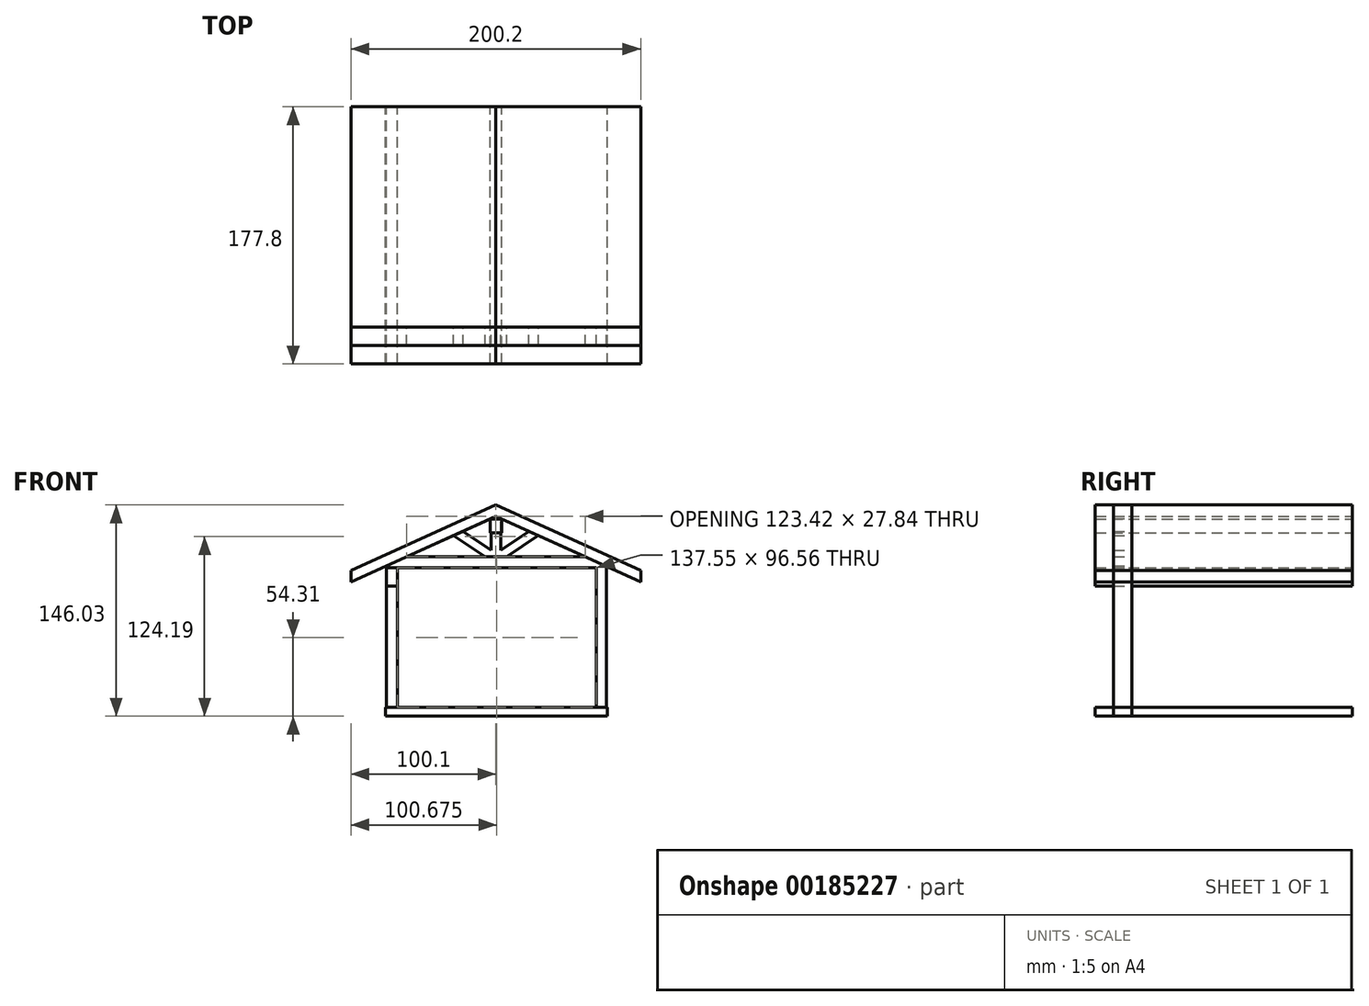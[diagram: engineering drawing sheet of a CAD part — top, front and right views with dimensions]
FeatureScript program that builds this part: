
annotation { "Feature Type Name" : "Feature", "Feature Type Description" : "" }
export const myFeature = defineFeature(function(context is Context, id is Id, definition is map)
    precondition{}
    {
        {
            var Q0;
            Q0=qCreatedBy(makeId("Front.planeOp"),FACE);
            var sketch = newSketch(context, id + "F0", { "sketchPlane" : qUnion([Q0])});
            skLineSegment(sketch, "E0.bottom", {"start": v(-76.23, -56.3) * mm, "end": v(77.09, -56.3) * mm});
            skLineSegment(sketch, "E0.top", {"start": v(-76.23, -62.33) * mm, "end": v(77.09, -62.33) * mm});
            skLineSegment(sketch, "E0.left", {"start": v(-76.23, -56.3) * mm, "end": v(-76.23, -62.33) * mm});
            skLineSegment(sketch, "E0.right", {"start": v(77.09, -56.3) * mm, "end": v(77.09, -62.33) * mm});
            skLineSegment(sketch, "E1.bottom", {"start": v(-75.65, 27.65) * mm, "end": v(-68.2, 27.65) * mm});
            skLineSegment(sketch, "E1.top", {"start": v(-75.65, -56.3) * mm, "end": v(-68.2, -56.3) * mm});
            skLineSegment(sketch, "E1.left", {"start": v(-75.65, 27.65) * mm, "end": v(-75.65, -56.3) * mm});
            skLineSegment(sketch, "E1.right", {"start": v(-68.2, 27.65) * mm, "end": v(-68.2, -56.3) * mm});
            skLineSegment(sketch, "E2.bottom", {"start": v(76.51, 25.93) * mm, "end": v(69.35, 25.93) * mm});
            skLineSegment(sketch, "E2.top", {"start": v(76.51, -56.3) * mm, "end": v(69.35, -56.3) * mm});
            skLineSegment(sketch, "E2.left", {"start": v(76.51, 25.93) * mm, "end": v(76.51, -56.3) * mm});
            skLineSegment(sketch, "E2.right", {"start": v(69.35, 25.93) * mm, "end": v(69.35, -56.3) * mm});
            skLineSegment(sketch, "E3.bottom", {"start": v(-75.65, 27.65) * mm, "end": v(-75.65, 27.65) * mm});
            skLineSegment(sketch, "E3.top", {"start": v(-75.65, 40.26) * mm, "end": v(-75.65, 40.26) * mm});
            skLineSegment(sketch, "E3.left", {"start": v(-75.65, 27.65) * mm, "end": v(-75.65, 40.26) * mm});
            skLineSegment(sketch, "E3.right", {"start": v(-75.65, 27.65) * mm, "end": v(-75.65, 40.26) * mm});
            skLineSegment(sketch, "E4.bottom", {"start": v(69.35, 40.26) * mm, "end": v(76.51, 40.26) * mm});
            skLineSegment(sketch, "E4.top", {"start": v(69.35, 25.93) * mm, "end": v(76.51, 25.93) * mm});
            skLineSegment(sketch, "E4.left", {"start": v(69.35, 40.26) * mm, "end": v(69.35, 25.93) * mm});
            skLineSegment(sketch, "E4.right", {"start": v(76.51, 40.26) * mm, "end": v(76.51, 25.93) * mm});
            skLineSegment(sketch, "E5.bottom", {"start": v(-75.65, 40.26) * mm, "end": v(76.51, 40.26) * mm});
            skLineSegment(sketch, "E5.top", {"start": v(-75.65, 47.94) * mm, "end": v(76.51, 47.94) * mm});
            skLineSegment(sketch, "E5.left", {"start": v(-75.65, 40.26) * mm, "end": v(-75.65, 47.94) * mm});
            skLineSegment(sketch, "E5.right", {"start": v(76.51, 40.26) * mm, "end": v(76.51, 47.94) * mm});
            skLineSegment(sketch, "E6", {"start": v(-68.2, 27.65) * mm, "end": v(-68.2, 40.26) * mm});
            skLineSegment(sketch, "E7", {"start": v(0, 75.78) * mm, "end": v(-100.1, 30.62) * mm});
            skLineSegment(sketch, "E8", {"start": v(0, 83.7) * mm, "end": v(-100.1, 38.55) * mm});
            skLineSegment(sketch, "E9", {"start": v(-100.1, 38.55) * mm, "end": v(-100.1, 30.62) * mm});
            skLineSegment(sketch, "E10", {"start": v(0, 83.7) * mm, "end": v(0, 75.78) * mm});
            skLineSegment(sketch, "E11.MirrorCS", {"start": v(0, 75.78) * mm, "end": v(100.1, 30.62) * mm});
            skLineSegment(sketch, "E12.MirrorCS", {"start": v(0, 83.7) * mm, "end": v(100.1, 38.55) * mm});
            skLineSegment(sketch, "E13.MirrorCS", {"start": v(100.1, 38.55) * mm, "end": v(100.1, 30.62) * mm});
            skLineSegment(sketch, "E14", {"start": v(-3.86, 74.04) * mm, "end": v(-3.86, 47.94) * mm});
            skLineSegment(sketch, "E15.MirrorCS", {"start": v(3.86, 74.04) * mm, "end": v(3.86, 47.94) * mm});
            skLineSegment(sketch, "E16", {"start": v(3.86, 51.44) * mm, "end": v(27.95, 63.17) * mm});
            skLineSegment(sketch, "E17", {"start": v(10.33, 47.94) * mm, "end": v(35.03, 59.97) * mm});
            skLineSegment(sketch, "E18.MirrorCS", {"start": v(-10.33, 47.94) * mm, "end": v(-35.03, 59.97) * mm});
            skLineSegment(sketch, "E19.MirrorCS", {"start": v(-3.86, 51.44) * mm, "end": v(-27.95, 63.17) * mm});
            skSolve(sketch);
        }
        {
            var Q0;
            Q0=qCreatedBy(makeId("Front.planeOp"),FACE);
            var sketch = newSketch(context, id + "F1", { "sketchPlane" : qUnion([Q0])});
            skLineSegment(sketch, "E20.bottom", {"start": v(-3.88, 74.12) * mm, "end": v(3.88, 74.12) * mm});
            skLineSegment(sketch, "E20.top", {"start": v(-3.88, 64.6) * mm, "end": v(3.88, 64.6) * mm});
            skLineSegment(sketch, "E20.left", {"start": v(-3.88, 74.12) * mm, "end": v(-3.88, 64.6) * mm});
            skLineSegment(sketch, "E20.right", {"start": v(3.88, 74.12) * mm, "end": v(3.88, 64.6) * mm});
            skSolve(sketch);
        }
        {
            var Q0;
            {var subQ0=sQuery(id+"F0.wireOp",EDGE,"E5.left");var subQ1=sQuery(id+"F0.wireOp",EDGE,"E5.top");var subQ2=makeQuery(id+"F0.imprint","INTERSECT",VERTEX,{"derivedFrom":[subQ1,subQ0]});Q0=makeQuery(id+"F0.imprint","IMPRINT",FACE,{"disambiguationData":[TD([[makeQuery(id+"F0.imprint","IMPRINT",EDGE,{"disambiguationData":[TD([[subQ2,-1.0]])],"derivedFrom":subQ1}),-1.0]])]});}
            var Q1;
            {var subQ0=sQuery(id+"F0.wireOp",EDGE,"E5.right");var subQ1=sQuery(id+"F0.wireOp",EDGE,"E5.top");var subQ2=makeQuery(id+"F0.imprint","INTERSECT",VERTEX,{"derivedFrom":[subQ1,subQ0]});Q1=makeQuery(id+"F0.imprint","IMPRINT",FACE,{"disambiguationData":[TD([[makeQuery(id+"F0.imprint","IMPRINT",EDGE,{"disambiguationData":[TD([[subQ2,1.0]])],"derivedFrom":subQ1}),-1.0]])]});}
            var Q2;
            Q2=makeQuery(id+"F0.imprint","IMPRINT",FACE,{"disambiguationData":[TD([[makeQuery(id+"F0.imprint","IMPRINT",EDGE,{"derivedFrom":sQuery(id+"F0.wireOp",EDGE,"E0.top")}),1.0]])]});
            var Q3;
            Q3=makeQuery(id+"F0.imprint","IMPRINT",FACE,{"disambiguationData":[TD([[makeQuery(id+"F0.imprint","IMPRINT",EDGE,{"derivedFrom":sQuery(id+"F0.wireOp",EDGE,"E1.bottom")}),1.0]])]});
            var Q4;
            Q4=makeQuery(id+"F0.imprint","IMPRINT",FACE,{"disambiguationData":[TD([[makeQuery(id+"F0.imprint","IMPRINT",EDGE,{"derivedFrom":sQuery(id+"F0.wireOp",EDGE,"E8")}),1.0]])]});
            var Q5;
            {var subQ5=sQuery(id+"F0.wireOp",EDGE,"E10");Q5=makeQuery(id+"F0.imprint","IMPRINT",FACE,{"disambiguationData":[TD([[makeQuery(id+"F0.imprint","IMPRINT",EDGE,{"derivedFrom":subQ5}),1.0]])]});}
            var Q6;
            Q6=makeQuery(id+"F0.imprint","IMPRINT",FACE,{"disambiguationData":[TD([[makeQuery(id+"F0.imprint","IMPRINT",EDGE,{"derivedFrom":sQuery(id+"F0.wireOp",EDGE,"E4.top")}),1.0]])]});
            var Q7;
            Q7=makeQuery(id+"F1.imprint","IMPRINT",FACE,{"disambiguationData":[TD([[makeQuery(id+"F1.imprint","IMPRINT",EDGE,{"derivedFrom":sQuery(id+"F1.wireOp",EDGE,"E20.bottom")}),-1.0]])]});
            extrude(context, id + "F2", {"entities" : qUnion([Q0, Q1, Q2, Q3, Q4, Q5, Q6, Q7]), "depth" : 25.4 * mm, "hasSecondDirection" : true, "secondDirectionOppositeDirection" : true, "secondDirectionDepth" : 152.4 * mm});
        }
        {
            var Q0;
            Q0 = qSketchRegion(id + "F0", true);
            extrude(context, id + "F3", {"entities" : qUnion([Q0]), "depth" : 12.7 * mm});
        }
        {
            var Q0;
            Q0=qCreatedBy(makeId("Front.planeOp"),FACE);
            var sketch = newSketch(context, id + "F4", { "sketchPlane" : qUnion([Q0])});
            skLineSegment(sketch, "E21.bottom", {"start": v(-2.91, 73.88) * mm, "end": v(2.91, 73.88) * mm});
            skLineSegment(sketch, "E21.top", {"start": v(-2.91, 61.53) * mm, "end": v(2.91, 61.53) * mm});
            skLineSegment(sketch, "E21.left", {"start": v(-2.91, 73.88) * mm, "end": v(-2.91, 61.53) * mm});
            skLineSegment(sketch, "E21.right", {"start": v(2.91, 73.88) * mm, "end": v(2.91, 61.53) * mm});
            skPoint(sketch, "E21.middle", {"position": v(0, 67.7) * mm});
            skLineSegment(sketch, "E22.top", {"start": v(-2.91, 47.98) * mm, "end": v(2.91, 47.98) * mm});
            skLineSegment(sketch, "E22.left", {"start": v(-2.91, 61.53) * mm, "end": v(-2.91, 47.98) * mm});
            skLineSegment(sketch, "E22.right", {"start": v(2.91, 61.53) * mm, "end": v(2.91, 47.98) * mm});
            skPoint(sketch, "E22.middle", {"position": v(0, 54.76) * mm});
            skLineSegment(sketch, "E23", {"start": v(-2.91, 54.76) * mm, "end": v(-24.85, 64.8) * mm});
            skLineSegment(sketch, "E24", {"start": v(-32.42, 61.11) * mm, "end": v(-3.75, 47.98) * mm});
            skLineSegment(sketch, "E25", {"start": v(-24.85, 64.8) * mm, "end": v(-32.42, 61.11) * mm});
            skLineSegment(sketch, "E26", {"start": v(-2.91, 54.76) * mm, "end": v(-2.91, 47.98) * mm});
            skLineSegment(sketch, "E27", {"start": v(-2.91, 47.98) * mm, "end": v(-3.75, 47.98) * mm});
            skLineSegment(sketch, "E28.MirrorCS", {"start": v(2.91, 54.76) * mm, "end": v(24.85, 64.8) * mm});
            skLineSegment(sketch, "E29.MirrorCS", {"start": v(32.42, 61.11) * mm, "end": v(3.75, 47.98) * mm});
            skSolve(sketch);
        }
        {
            var Q0;
            {var subQ1=sQuery(id+"F4.wireOp",EDGE,"E21.top");Q0=makeQuery(id+"F4.imprint","IMPRINT",FACE,{"disambiguationData":[TD([[makeQuery(id+"F4.imprint","IMPRINT",EDGE,{"derivedFrom":subQ1}),-1.0]])]});}
            var sketch = newSketch(context, id + "F5", { "sketchPlane" : qUnion([Q0])});
            skLineSegment(sketch, "E30", {"start": v(2.82, 54.9) * mm, "end": v(2.82, 48.14) * mm});
            skLineSegment(sketch, "E31", {"start": v(2.82, 48.14) * mm, "end": v(2.82, 48.14) * mm});
            skLineSegment(sketch, "E32", {"start": v(24.6, 64.8) * mm, "end": v(31.47, 61.1) * mm});
            skLineSegment(sketch, "E33", {"start": v(-24.82, 64.47) * mm, "end": v(-32.42, 61.11) * mm});
            skLineSegment(sketch, "E34", {"start": v(-3.69, 48.1) * mm, "end": v(-3.69, 54.9) * mm});
            skLineSegment(sketch, "E35", {"start": v(-3.69, 54.9) * mm, "end": v(-24.82, 64.47) * mm});
            skLineSegment(sketch, "E36", {"start": v(-32.42, 61.11) * mm, "end": v(-3.69, 48.1) * mm});
            skLineSegment(sketch, "E37", {"start": v(2.82, 54.9) * mm, "end": v(24.6, 64.8) * mm});
            skLineSegment(sketch, "E38", {"start": v(2.82, 48.14) * mm, "end": v(31.47, 61.1) * mm});
            skLineSegment(sketch, "E39", {"start": v(-3.69, 74.12) * mm, "end": v(-3.69, 48.14) * mm});
            skLineSegment(sketch, "E40", {"start": v(2.82, 73.92) * mm, "end": v(2.82, 48.14) * mm});
            skLineSegment(sketch, "E41", {"start": v(-3.69, 74.12) * mm, "end": v(2.82, 73.92) * mm});
            skLineSegment(sketch, "E42", {"start": v(-3.69, 61.1) * mm, "end": v(2.82, 61.1) * mm});
            skLineSegment(sketch, "E43", {"start": v(-3.69, 48.14) * mm, "end": v(2.82, 48.14) * mm});
            skLineSegment(sketch, "E44.MirrorCS", {"start": v(32.42, 61.11) * mm, "end": v(3.69, 48.1) * mm});
            skLineSegment(sketch, "E45.MirrorCS", {"start": v(3.69, 54.9) * mm, "end": v(24.82, 64.47) * mm});
            skLineSegment(sketch, "E46.MirrorCS", {"start": v(3.69, 74.12) * mm, "end": v(3.69, 48.14) * mm});
            skLineSegment(sketch, "E47.MirrorCS", {"start": v(3.69, 61.1) * mm, "end": v(-2.82, 61.1) * mm});
            skLineSegment(sketch, "E48.MirrorCS", {"start": v(3.69, 74.12) * mm, "end": v(-2.82, 73.92) * mm});
            skSolve(sketch);
        }
        {
            var Q0;
            Q0 = qSketchRegion(id + "F5", true);
            var Q1;
            Q1=makeQuery(id+"F4.imprint","IMPRINT",FACE,{"disambiguationData":[TD([[makeQuery(id+"F4.imprint","IMPRINT",EDGE,{"derivedFrom":sQuery(id+"F4.wireOp",EDGE,"E21.bottom")}),-1.0]])]});
            extrude(context, id + "F6", {"entities" : qUnion([Q0, Q1]), "depth" : 12.7 * mm});
        }
        {
            var Q0;
            Q0=makeQuery(id+"F6.opExtrude","SWEPT_BODY",BODY,{"disambiguationData":[OSD([sQuery(id+"F5.wireOp",EDGE,"E32"),sQuery(id+"F5.wireOp",EDGE,"E33"),sQuery(id+"F5.wireOp",EDGE,"E34"),sQuery(id+"F5.wireOp",EDGE,"E35"),sQuery(id+"F5.wireOp",EDGE,"E36"),sQuery(id+"F5.wireOp",EDGE,"E37"),sQuery(id+"F5.wireOp",EDGE,"E38"),sQuery(id+"F5.wireOp",EDGE,"E39"),sQuery(id+"F5.wireOp",EDGE,"E41"),sQuery(id+"F5.wireOp",EDGE,"E43"),sQuery(id+"F5.wireOp",EDGE,"E46.MirrorCS"),sQuery(id+"F5.wireOp",EDGE,"E48.MirrorCS")])]});
            deleteBodies(context, id + "F7", {"entities" : qUnion([Q0])});
        }
        {
            var Q0;
            Q0=makeQuery(id+"F6.opExtrude","SWEPT_BODY",BODY,{"disambiguationData":[OSD([sQuery(id+"F4.wireOp",EDGE,"E21.bottom"),sQuery(id+"F4.wireOp",EDGE,"E21.left"),sQuery(id+"F4.wireOp",EDGE,"E21.right"),sQuery(id+"F4.wireOp",EDGE,"E21.top")])]});
            deleteBodies(context, id + "F8", {"entities" : qUnion([Q0])});
        }
        {
            var Q0;
            Q0=qCreatedBy(makeId("Front.planeOp"),FACE);
            var sketch = newSketch(context, id + "F9", { "sketchPlane" : qUnion([Q0])});
            skLineSegment(sketch, "E49.bottom", {"start": v(-3.3, 48.1) * mm, "end": v(3.3, 48.1) * mm});
            skLineSegment(sketch, "E49.top", {"start": v(-3.3, 76.83) * mm, "end": v(3.3, 76.83) * mm});
            skLineSegment(sketch, "E49.left", {"start": v(-3.3, 48.1) * mm, "end": v(-3.3, 76.83) * mm});
            skLineSegment(sketch, "E49.right", {"start": v(3.3, 48.1) * mm, "end": v(3.3, 76.83) * mm});
            skPoint(sketch, "E49.middle", {"position": v(0, 62.47) * mm});
            skLineSegment(sketch, "E50", {"start": v(-3.3, 52.38) * mm, "end": v(-22.67, 65.35) * mm});
            skLineSegment(sketch, "E51", {"start": v(-7.57, 48.1) * mm, "end": v(-29.31, 62.66) * mm});
            skLineSegment(sketch, "E52", {"start": v(-7.57, 48.1) * mm, "end": v(-3.3, 48.1) * mm});
            skLineSegment(sketch, "E53", {"start": v(-29.31, 62.66) * mm, "end": v(-22.67, 65.35) * mm});
            skLineSegment(sketch, "E54.MirrorCS", {"start": v(7.57, 48.1) * mm, "end": v(29.31, 62.66) * mm});
            skLineSegment(sketch, "E55.MirrorCS", {"start": v(3.3, 52.38) * mm, "end": v(22.67, 65.35) * mm});
            skLineSegment(sketch, "E56.MirrorCS", {"start": v(29.31, 62.66) * mm, "end": v(22.67, 65.35) * mm});
            skLineSegment(sketch, "E57.MirrorCS", {"start": v(7.57, 48.1) * mm, "end": v(3.3, 48.1) * mm});
            skLineSegment(sketch, "E58", {"start": v(-3.3, 65.58) * mm, "end": v(3.3, 65.58) * mm});
            skLineSegment(sketch, "E59", {"start": v(-3.3, 74.16) * mm, "end": v(0, 75.8) * mm});
            skLineSegment(sketch, "E60.MirrorCS", {"start": v(3.3, 74.16) * mm, "end": v(0, 75.8) * mm});
            skSolve(sketch);
        }
        {
            var Q0;
            {var subQ1=sQuery(id+"F9.wireOp",EDGE,"E50");Q0=makeQuery(id+"F9.imprint","IMPRINT",FACE,{"disambiguationData":[TD([[makeQuery(id+"F9.imprint","IMPRINT",EDGE,{"derivedFrom":subQ1}),1.0]])]});}
            var Q1;
            {var subQ1=sQuery(id+"F9.wireOp",EDGE,"E49.bottom");Q1=makeQuery(id+"F9.imprint","IMPRINT",FACE,{"disambiguationData":[TD([[makeQuery(id+"F9.imprint","IMPRINT",EDGE,{"derivedFrom":subQ1}),1.0]])]});}
            var Q2;
            Q2=makeQuery(id+"F9.imprint","IMPRINT",FACE,{"disambiguationData":[TD([[makeQuery(id+"F9.imprint","IMPRINT",EDGE,{"derivedFrom":sQuery(id+"F9.wireOp",EDGE,"E54.MirrorCS")}),1.0]])]});
            var Q3;
            {var subQ0=sQuery(id+"F9.wireOp",EDGE,"E58");Q3=makeQuery(id+"F9.imprint","IMPRINT",FACE,{"disambiguationData":[TD([[makeQuery(id+"F9.imprint","IMPRINT",EDGE,{"derivedFrom":subQ0}),1.0]])]});}
            extrude(context, id + "F10", {"entities" : qUnion([Q0, Q1, Q2, Q3]), "depth" : 12.7 * mm});
        }
    });
